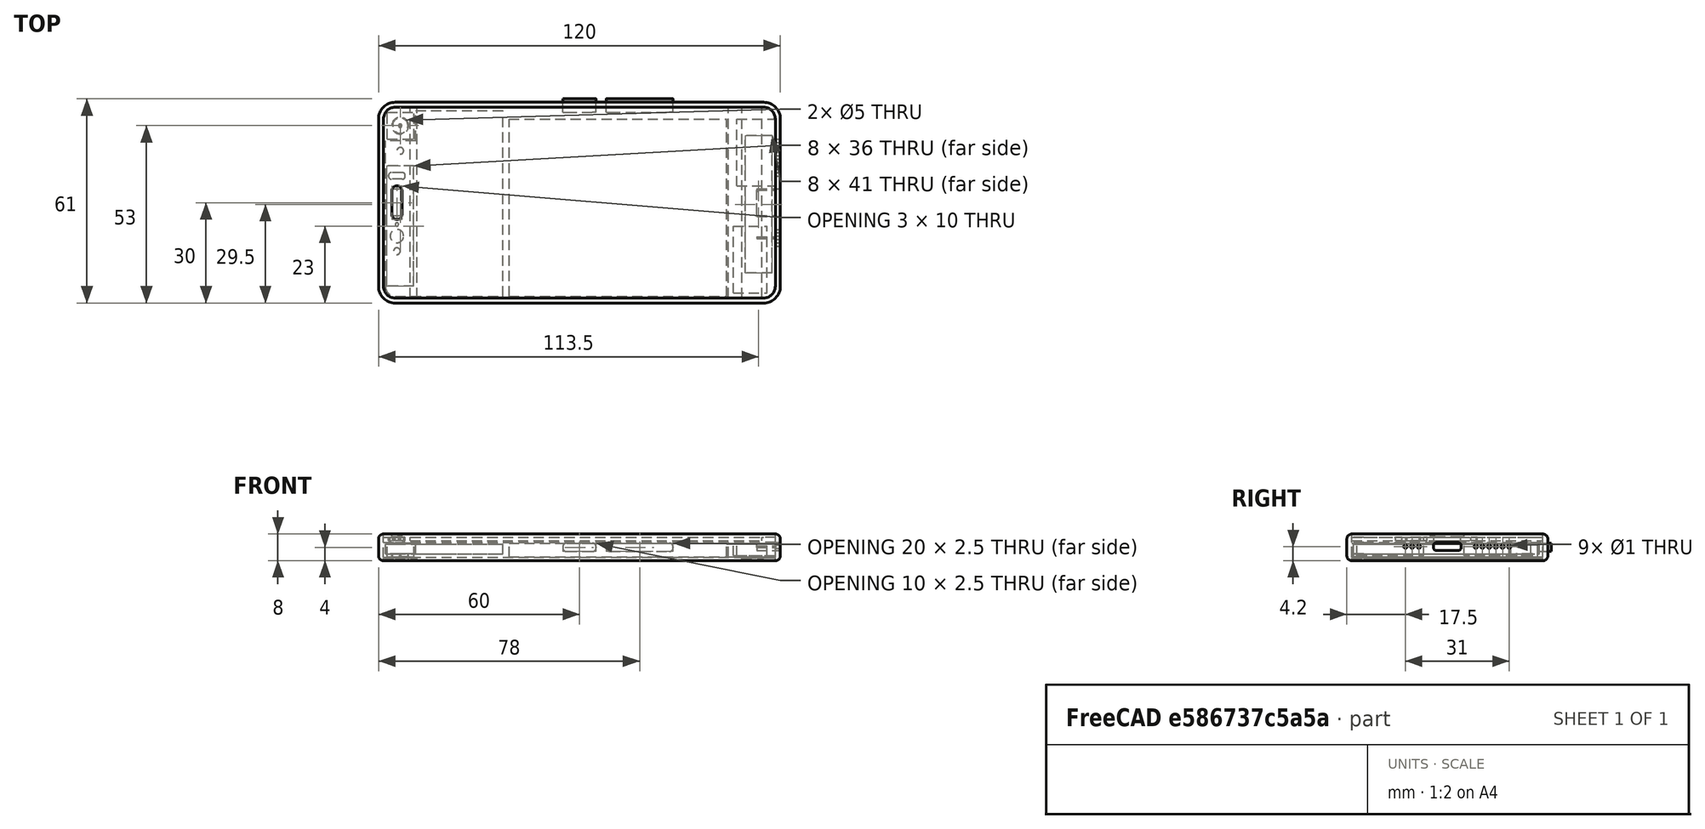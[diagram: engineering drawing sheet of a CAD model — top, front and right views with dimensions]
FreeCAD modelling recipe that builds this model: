
FCSTD DOCUMENT  (FreeCAD 0.16R6706 (Git))
Label: device
License: All rights reserved
LicenseURL: http://en.wikipedia.org/wiki/All_rights_reserved
objects: Part::Box×30, Part::Fillet×20, Part::Cut×20, Part::Cylinder×19, Part::MultiFuse×13, Part::Sphere×2
note: 104 computed .brp shape members not serialized (recipe doc carries the construction recipe); baked Part::Feature solids carry a one-line shape summary decoded from their .brp

FEATURE [Part::Box] Box  label="Cubo"
  Height = 8
  Length = 120
  Width = 60
FEATURE [Part::Box] Box001  label="Cubo001"
  Height = 8
  Length = 117
  Placement = pos=(1.5,1.5,0) rot=(0,0,1;0rad)
  Width = 57
FEATURE [Part::Fillet] Fillet
  Base = -> Box
  Edges = 4 edges r=5: [Edge1,Edge3,Edge5,Edge7]
FEATURE [Part::Fillet] Fillet001
  Base = -> Fillet
  Edges = 16 edges r=1.5: [Edge1,Edge4,Edge5,Edge6,Edge7,Edge8,Edge9,Edge10,Edge11,Edge12,Edge14,Edge16,Edge17,Edge18,Edge19,Edge20]
FEATURE [Part::Fillet] Fillet002
  Base = -> Box001
  Edges = 4 edges r=3.5: [Edge1,Edge3,Edge5,Edge7]
  Placement = pos=(0,0,1) rot=(0,0,1;0rad)
FEATURE [Part::Box] Box002  label="Cubo002"
  Height = 1
  Length = 117
  Placement = pos=(1.5,1.5,0) rot=(0,0,1;0rad)
  Width = 57
FEATURE [Part::Fillet] Fillet003
  Base = -> Box002
  Edges = 4 edges r=3.5: [Edge1,Edge3,Edge5,Edge7]
  Placement = pos=(0,0,7) rot=(0,0,1;0rad)
FEATURE [Part::Cut] Cut
  Base = -> Fillet001
  Tool = -> Fillet002
FEATURE [Part::Box] Box003  label="Cubo003"
  Height = 1
  Length = 8
  Placement = pos=(1.5,1.5,0) rot=(0,0,1;0rad)
  Width = 57
FEATURE [Part::Box] Box004  label="Cubo004"
  Height = 1
  Length = 4
  Placement = pos=(114.5,1.5,0) rot=(0,0,1;0rad)
  Width = 57
FEATURE [Part::MultiFuse] Fusion
  Placement = pos=(0,0,6) rot=(0,0,1;0rad)
  Shapes = -> [Box004,Box003]
FEATURE [Part::Fillet] Fillet004
  Base = -> Fusion
  Edges = 4 edges r=3.5: [Edge5,Edge7,Edge13,Edge15]
FEATURE [Part::Box] Box005  label="Screen"
  Height = 1
  Length = 105
  Placement = pos=(9.5,1.5,6) rot=(0,0,1;0rad)
  Width = 57
FEATURE [Part::Box] Box006  label="Cubo006"
  Height = 0.5
  Length = 117
  Placement = pos=(1.5,1.5,0) rot=(0,0,1;0rad)
  Width = 57
FEATURE [Part::Fillet] Fillet005
  Base = -> Box006
  Edges = 4 edges r=3.5: [Edge1,Edge3,Edge5,Edge7]
  Placement = pos=(0,0,5.5) rot=(0,0,1;0rad)
FEATURE [Part::Box] Box007  label="Cubo007"
  Height = 10
  Length = 3
  Placement = pos=(4,25,0) rot=(0,0,1;0rad)
  Width = 10
FEATURE [Part::Fillet] Fillet006
  Base = -> Box007
  Edges = 4 edges r=1.4: [Edge1,Edge3,Edge5,Edge7]
FEATURE [Part::Cut] Cut001  label="TouchScreen"
  Base = -> Fillet003
  Tool = -> Fillet006
FEATURE [Part::Box] Box009  label="Cubo009"
  Height = 10
  Length = 5
  Placement = pos=(3,37,0) rot=(0,0,1;0rad)
  Width = 2
FEATURE [Part::Fillet] Fillet007
  Base = -> Box009
  Edges = 4 edges r=0.9: [Edge1,Edge3,Edge5,Edge7]
FEATURE [Part::Cut] Cut002
  Base = -> Fillet004
  Tool = -> Fillet007
FEATURE [Part::Cylinder] Cylinder  label="Cilindro"
  Angle = 360
  Height = 10
  Placement = pos=(5.5,20,0) rot=(0,0,1;0rad)
  Radius = 2
FEATURE [Part::Cut] Cut003
  Base = -> Cut002
  Tool = -> Cylinder
FEATURE [Part::Cylinder] Cylinder003  label="Cilindro002"
  Angle = 360
  Height = 10
  Placement = pos=(5.5,23.5,0) rot=(0,0,1;0rad)
  Radius = 0.5
FEATURE [Part::Cut] Cut004
  Base = -> Cut003
  Tool = -> Cylinder003
FEATURE [Part::Cylinder] Cylinder004  label="Cilindro003"
  Angle = 360
  Height = 10
  Placement = pos=(5.5,15.5,0) rot=(0,0,1;0rad)
  Radius = 1
FEATURE [Part::Cut] Cut006
  Base = -> Cut004
  Tool = -> Cylinder004
FEATURE [Part::Cylinder] Cylinder005  label="Camera001"
  Angle = 360
  Height = 10
  Placement = pos=(6.5,53,-3) rot=(0,0,1;0rad)
  Radius = 2.5
FEATURE [Part::Cylinder] Cylinder006  label="Flash"
  Angle = 360
  Height = 10
  Placement = pos=(6.5,45.5,-3) rot=(0,0,1;0rad)
  Radius = 1
FEATURE [Part::MultiFuse] Fusion001  label="Camera"
  Shapes = -> [Cylinder005,Cylinder006]
FEATURE [Part::Cylinder] Cylinder007  label="Camera lent"
  Angle = 360
  Height = 1
  Placement = pos=(6.5,53,0) rot=(0,0,1;0rad)
  Radius = 2.5
FEATURE [Part::Cut] Cut007
  Base = -> Cut
  Tool = -> Fusion001
FEATURE [Part::Cylinder] Cylinder008  label="Flash lens"
  Angle = 360
  Height = 1
  Placement = pos=(6.5,45.5,0) rot=(0,0,1;0rad)
  Radius = 1
FEATURE [Part::Box] Box010  label="Cubo010"
  Height = 0.2
  Length = 3
  Placement = pos=(4,25,0) rot=(0,0,1;0rad)
  Width = 10
FEATURE [Part::Fillet] Fillet008  label="Speaker bezel"
  Base = -> Box010
  Edges = 4 edges r=1.4: [Edge1,Edge3,Edge5,Edge7]
  Placement = pos=(0,0,7) rot=(0,0,1;0rad)
FEATURE [Part::Box] Box011  label="Cubo011"
  Height = 10
  Length = 2.5
  Placement = pos=(4.2,26,0) rot=(0,0,1;0rad)
  Width = 8
FEATURE [Part::Cut] Cut008
  Base = -> Cut006
  Tool = -> Box011
FEATURE [Part::Box] Box012  label="Back Camera"
  Height = 4.2
  Length = 8
  Placement = pos=(2.6,49,1.2) rot=(0,0,1;0rad)
  Width = 8
FEATURE [Part::Box] Box013  label="Cubo013"
  Height = 3
  Length = 35
  Placement = pos=(2.1,2,2.5) rot=(0,0,1;0rad)
  Width = 55.5
FEATURE [Part::Fillet] Fillet009
  Base = -> Box013
  Edges = 1 edges r=3: [Edge1]
FEATURE [Part::Box] Box014  label="Back Camera001"
  Height = 4.2
  Length = 9
  Placement = pos=(2.1,48.5,1.6) rot=(0,0,1;0rad)
  Width = 9
FEATURE [Part::Cut] Cut009  label="PCB"
  Base = -> Fillet009
  Placement = pos=(0,0,-0.5) rot=(0,0,1;0rad)
  Tool = -> Box014
FEATURE [Part::Box] Box015  label="Battery"
  Height = 4
  Length = 65
  Placement = pos=(39,2,1.2) rot=(0,0,1;0rad)
  Width = 53
FEATURE [Part::Box] Box016  label="Cubo015"
  Height = 4
  Length = 14
  Placement = pos=(104.5,1.5,1.2) rot=(0,0,1;0rad)
  Width = 57
FEATURE [Part::Fillet] Fillet010
  Base = -> Box016
  Edges = 2 edges r=3.5: [Edge5,Edge7]
FEATURE [Part::MultiFuse] Fusion002  label="Frame"
  Shapes = -> [Fillet005,Cut008]
FEATURE [Part::Cylinder] Cylinder009  label="Camera lent001"
  Angle = 360
  Height = 1
  Placement = pos=(6.5,53,1) rot=(0,0,1;0rad)
  Radius = 2.5
FEATURE [Part::Cut] Cut010  label="Camera002"
  Base = -> Box012
  Tool = -> Cylinder009
FEATURE [Part::Cylinder] Cylinder010  label="Camera lent002"
  Angle = 360
  Height = 1
  Placement = pos=(6.5,53,1) rot=(0,0,1;0rad)
  Radius = 2.3
FEATURE [Part::Sphere] Sphere001  label="Esfera"
  Angle1 = -90
  Angle2 = 90
  Angle3 = 360
  Placement = pos=(6.5,53,1) rot=(0,0,1;0rad)
  Radius = 0.5
FEATURE [Part::Cut] Cut011
  Base = -> Cylinder007
  Tool = -> Sphere001
FEATURE [Part::Sphere] Sphere002  label="Esfera001"
  Angle1 = -90
  Angle2 = 90
  Angle3 = 360
  Placement = pos=(6.5,53,1) rot=(0,0,1;0rad)
  Radius = 0.5
FEATURE [Part::Box] Box035  label="Cubo029"
  Height = 2.45
  Length = 8.65
  Width = 8.3
FEATURE [Part::Fillet] Fillet022  label="USB-C"
  Base = -> Box035
  Edges = 4 edges r=1: [Edge9,Edge10,Edge11,Edge12]
  Placement = pos=(113,25.85,3) rot=(0,0,1;0rad)
FEATURE [Part::Cylinder] Cylinder011  label="Cilindro004"
  Angle = 360
  Height = 10
  Placement = pos=(113,48.5,4.2) rot=(0.57735,0.57735,0.57735;2.0944rad)
  Radius = 0.5
FEATURE [Part::Cylinder] Cylinder012  label="Cilindro005"
  Angle = 360
  Height = 10
  Placement = pos=(113,11.5,4.2) rot=(0.57735,0.57735,0.57735;2.0944rad)
  Radius = 0.5
FEATURE [Part::Cylinder] Cylinder013  label="Cilindro006"
  Angle = 360
  Height = 10
  Placement = pos=(113,46.5,4.2) rot=(0.57735,0.57735,0.57735;2.0944rad)
  Radius = 0.5
FEATURE [Part::Cylinder] Cylinder014  label="Cilindro007"
  Angle = 360
  Height = 10
  Placement = pos=(113,13.5,4.2) rot=(0.57735,0.57735,0.57735;2.0944rad)
  Radius = 0.5
FEATURE [Part::Cylinder] Cylinder015  label="Cilindro008"
  Angle = 360
  Height = 10
  Placement = pos=(113,44.5,4.2) rot=(0.57735,0.57735,0.57735;2.0944rad)
  Radius = 0.5
FEATURE [Part::Cylinder] Cylinder016  label="Cilindro009"
  Angle = 360
  Height = 10
  Placement = pos=(113,15.5,4.2) rot=(0.57735,0.57735,0.57735;2.0944rad)
  Radius = 0.5
FEATURE [Part::MultiFuse] Fusion003  label="mic holes"
  Placement = pos=(0,6,0) rot=(0,0,1;0rad)
  Shapes = -> [Cylinder012,Cylinder014,Cylinder016]
FEATURE [Part::MultiFuse] Fusion004
  Placement = pos=(0,-6,0) rot=(0,0,1;0rad)
  Shapes = -> [Cylinder013,Cylinder011,Cylinder015]
FEATURE [Part::Cylinder] Cylinder017  label="Cilindro010"
  Angle = 360
  Height = 10
  Placement = pos=(113,48.5,4.2) rot=(0.57735,0.57735,0.57735;2.0944rad)
  Radius = 0.5
FEATURE [Part::Cylinder] Cylinder018  label="Cilindro011"
  Angle = 360
  Height = 10
  Placement = pos=(113,46.5,4.2) rot=(0.57735,0.57735,0.57735;2.0944rad)
  Radius = 0.5
FEATURE [Part::Cylinder] Cylinder019  label="Cilindro012"
  Angle = 360
  Height = 10
  Placement = pos=(113,44.5,4.2) rot=(0.57735,0.57735,0.57735;2.0944rad)
  Radius = 0.5
FEATURE [Part::MultiFuse] Fusion005
  Shapes = -> [Cylinder018,Cylinder017,Cylinder019]
FEATURE [Part::MultiFuse] Fusion006  label="speaker holes"
  Shapes = -> [Fusion005,Fusion004]
FEATURE [Part::MultiFuse] Fusion007  label="Bot holes"
  Shapes = -> [Fusion003,Fillet022,Fusion006]
FEATURE [Part::Cut] Cut012
  Base = -> Cut007
  Tool = -> Fusion007
FEATURE [Part::Cut] Cut013
  Base = -> Fillet010
  Tool = -> Fillet022
FEATURE [Part::Cylinder] Cylinder020  label="Cilindro013"
  Angle = 360
  Height = 10
  Placement = pos=(113,19.5,4.2) rot=(0.57735,0.57735,0.57735;2.0944rad)
  Radius = 0.25
FEATURE [Part::Cut] Cut014
  Base = -> Cut013
  Tool = -> Cylinder020
FEATURE [Part::Box] Box036  label="Tapic engine"
  Height = 3.7
  Length = 10
  Placement = pos=(106,3,1.5) rot=(0,0,1;0rad)
  Width = 20
FEATURE [Part::Box] Box037  label="Speaker hole"
  Height = 3.7
  Length = 14
  Placement = pos=(107,35,1.5) rot=(0,0,1;0rad)
  Width = 20
FEATURE [Part::Cut] Cut015  label="Buzzer"
  Base = -> Cut014
  Tool = -> Box037
FEATURE [Part::Box] Box038  label="Speaker"
  Height = 3.7
  Length = 11.5
  Placement = pos=(107,35,1.5) rot=(0,0,1;0rad)
  Width = 20
FEATURE [Part::Box] Box039  label="Cubo030"
  Height = 0.8
  Length = 10
  Placement = pos=(1.5,1.5,0) rot=(0,0,1;0rad)
  Width = 57
FEATURE [Part::Fillet] Fillet023
  Base = -> Box039
  Edges = 2 edges r=3.5: [Edge1,Edge3]
FEATURE [Part::Box] Box041  label="Cubo031"
  Height = 0.8
  Length = 10
  Placement = pos=(108.5,1.5,0) rot=(0,0,1;0rad)
  Width = 57
FEATURE [Part::Fillet] Fillet024
  Base = -> Box041
  Edges = 2 edges r=3.5: [Edge5,Edge7]
FEATURE [Part::MultiFuse] Fusion008
  Shapes = -> [Fillet023,Fillet024]
FEATURE [Part::Box] Box042  label="Cubo032"
  Height = 0.8
  Length = 10
  Placement = pos=(1.5,1.5,0) rot=(0,0,1;0rad)
  Width = 57
FEATURE [Part::Fillet] Fillet025
  Base = -> Box042
  Edges = 2 edges r=3.5: [Edge1,Edge3]
FEATURE [Part::Box] Box043  label="Cubo033"
  Height = 0.8
  Length = 10
  Placement = pos=(108.5,1.5,0) rot=(0,0,1;0rad)
  Width = 57
FEATURE [Part::Fillet] Fillet026
  Base = -> Box043
  Edges = 2 edges r=3.5: [Edge5,Edge7]
FEATURE [Part::MultiFuse] Fusion009
  Shapes = -> [Fillet025,Fillet026]
FEATURE [Part::Cut] Cut016
  Base = -> Cut012
  Tool = -> Fusion008
FEATURE [Part::Cut] Cut017
  Base = -> Fusion009
  Tool = -> Cut011
FEATURE [Part::Cut] Cut018  label="Antenna"
  Base = -> Cut017
  Tool = -> Cylinder008
FEATURE [Part::Box] Box044  label="Cubo034"
  Height = 10
  Length = 8
  Placement = pos=(2.5,5,0) rot=(0,0,1;0rad)
  Width = 36
FEATURE [Part::Box] Box045  label="Cubo035"
  Height = 10
  Length = 8
  Placement = pos=(109.5,9,0) rot=(0,0,1;0rad)
  Width = 41
FEATURE [Part::MultiFuse] Fusion010
  Shapes = -> [Box045,Box044]
FEATURE [Part::Cut] Cut019  label="Cut018"
  Base = -> Cut016
  Tool = -> Fusion010
FEATURE [Part::Box] Box046  label="Cubo036"
  Height = 2.5
  Length = 10
  Placement = pos=(55,57,2.75) rot=(0,0,1;0rad)
  Width = 4
FEATURE [Part::Box] Box047  label="Cubo037"
  Height = 2.5
  Length = 20
  Placement = pos=(68,57,2.75) rot=(0,0,1;0rad)
  Width = 4
FEATURE [Part::Fillet] Fillet027  label="PowerButtonr"
  Base = -> Box046
  Edges = 4 edges r=1.2: [Edge2,Edge4,Edge6,Edge8]
FEATURE [Part::Fillet] Fillet028  label="VolumeButtonr"
  Base = -> Box047
  Edges = 4 edges r=1.2: [Edge2,Edge4,Edge6,Edge8]
FEATURE [Part::MultiFuse] Fusion011  label="Buttonsr"
  Shapes = -> [Fillet027,Fillet028]
FEATURE [Part::Cut] Cut020  label="Chassis"
  Base = -> Cut019
  Tool = -> Fusion011
FEATURE [Part::Box] Box048  label="Cubo038"
  Height = 2.5
  Length = 10
  Placement = pos=(55,57,2.75) rot=(0,0,1;0rad)
  Width = 4
FEATURE [Part::Box] Box049  label="Cubo039"
  Height = 2.5
  Length = 20
  Placement = pos=(68,57,2.75) rot=(0,0,1;0rad)
  Width = 4
FEATURE [Part::Fillet] Fillet029  label="PowerButton"
  Base = -> Box048
  Edges = 4 edges r=1.2: [Edge2,Edge4,Edge6,Edge8]
FEATURE [Part::Fillet] Fillet030  label="VolumeButton"
  Base = -> Box049
  Edges = 4 edges r=1.2: [Edge2,Edge4,Edge6,Edge8]
FEATURE [Part::MultiFuse] Fusion012  label="Buttons"
  Shapes = -> [Fillet029,Fillet030]
